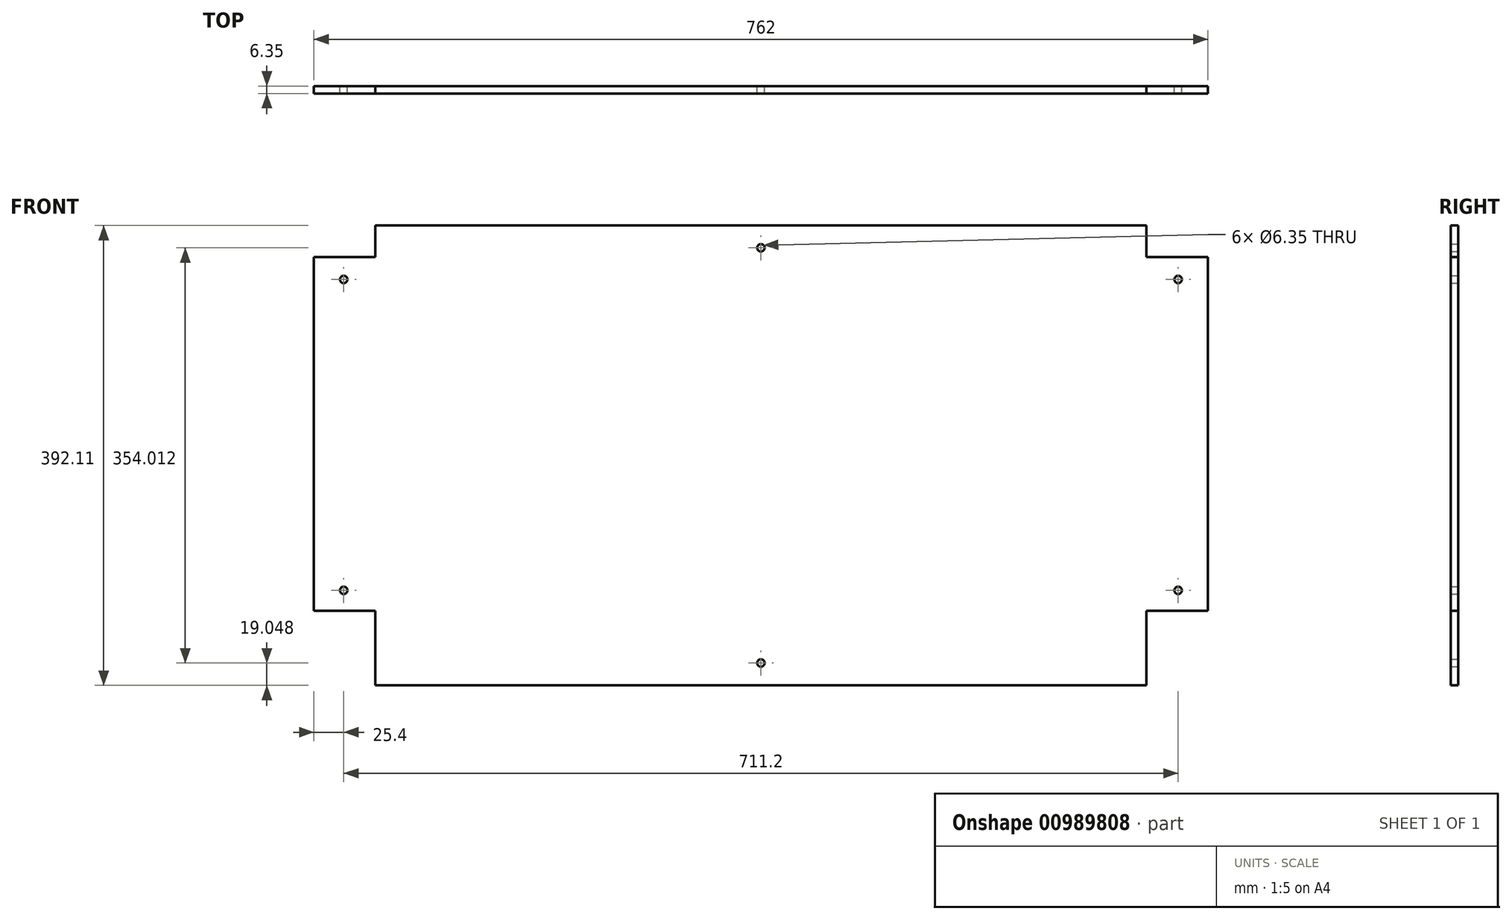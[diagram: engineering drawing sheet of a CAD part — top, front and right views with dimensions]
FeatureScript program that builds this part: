
annotation { "Feature Type Name" : "Feature", "Feature Type Description" : "" }
export const myFeature = defineFeature(function(context is Context, id is Id, definition is map)
    precondition{}
    {
        {
            var Q0;
            Q0=qCreatedBy(makeId("Front.planeOp"),FACE);
            var sketch = newSketch(context, id + "F0", { "sketchPlane" : qUnion([Q0])});
            skLineSegment(sketch, "E0.bottom", {"start": v(-381, 150.81) * mm, "end": v(-328.61, 150.81) * mm});
            skLineSegment(sketch, "E0.top", {"start": v(-381, -150.81) * mm, "end": v(-328.61, -150.81) * mm});
            skLineSegment(sketch, "E0.left", {"start": v(-381, 150.81) * mm, "end": v(-381, -150.81) * mm});
            skLineSegment(sketch, "E0.right", {"start": v(381, 150.81) * mm, "end": v(381, -150.81) * mm});
            skLineSegment(sketch, "E1.top", {"start": v(-328.61, -214.31) * mm, "end": v(328.61, -214.31) * mm});
            skLineSegment(sketch, "E1.left", {"start": v(-328.61, -150.81) * mm, "end": v(-328.61, -214.31) * mm});
            skLineSegment(sketch, "E1.right", {"start": v(328.61, -150.81) * mm, "end": v(328.61, -214.31) * mm});
            skLineSegment(sketch, "E2.top", {"start": v(-328.61, 177.8) * mm, "end": v(328.61, 177.8) * mm});
            skLineSegment(sketch, "E2.left", {"start": v(-328.61, 150.81) * mm, "end": v(-328.61, 177.8) * mm});
            skLineSegment(sketch, "E2.right", {"start": v(328.61, 150.81) * mm, "end": v(328.61, 177.8) * mm});
            skLineSegment(sketch, "E3.trimOffspring", {"start": v(328.61, -150.81) * mm, "end": v(381, -150.81) * mm});
            skLineSegment(sketch, "E4.trimOffspring", {"start": v(328.61, 150.81) * mm, "end": v(381, 150.81) * mm});
            skCircle(sketch, "E5", {"center": v(-355.6, 131.76) * mm, "radius": 3.18 * mm});
            skCircle(sketch, "E6.0.1.0", {"center": v(-355.6, -133.35) * mm, "radius": 3.18 * mm});
            skCircle(sketch, "E6.1.0.0", {"center": v(355.6, 131.76) * mm, "radius": 3.18 * mm});
            skCircle(sketch, "E6.1.1.0", {"center": v(355.6, -133.35) * mm, "radius": 3.18 * mm});
            skLineSegment(sketch, "E6.direction1", {"start": v(-355.6, 131.76) * mm, "end": v(355.6, 131.76) * mm, "construction": true});
            skLineSegment(sketch, "E6.direction2", {"start": v(-355.6, 131.76) * mm, "end": v(-355.6, -133.35) * mm, "construction": true});
            skCircle(sketch, "E7", {"center": v(0, 158.75) * mm, "radius": 3.18 * mm});
            skCircle(sketch, "E8", {"center": v(0, -195.26) * mm, "radius": 3.18 * mm});
            skSolve(sketch);
        }
        {
            var Q0;
            Q0=makeQuery(id+"F0.imprint","IMPRINT",FACE,{"disambiguationData":[TD([[makeQuery(id+"F0.imprint","IMPRINT",EDGE,{"derivedFrom":sQuery(id+"F0.wireOp",EDGE,"E0.bottom")}),-1.0]])]});
            extrude(context, id + "F1", {"entities" : qUnion([Q0]), "depth" : 6.35 * mm, "offsetDistance" : 25.4 * mm});
        }
    });
